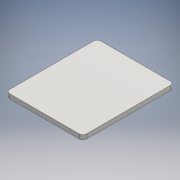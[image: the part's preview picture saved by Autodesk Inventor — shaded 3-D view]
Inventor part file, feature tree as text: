
AUTODESK INVENTOR PART (.ipt)
format: ipt  version: 2016 (Build 200138000, 138)  size: 102,400 bytes
history: native  units: mm
features: extrude x1, sketch x1
ambient origin geometry x8: Origin, YZ Plane, XZ Plane, XY Plane, X Axis, Y Axis, Z Axis, Center Point
bodies: Solid1 (feature_tree)
feature tree (2):
  extrude  "Extrusion1"  Depth=51.0mm
  sketch  "Sketch1"  dims[d0=43.0mm d1=51.0mm d2=2.0mm d3=2.0mm d4=2.5mm d5=0.0mm]
